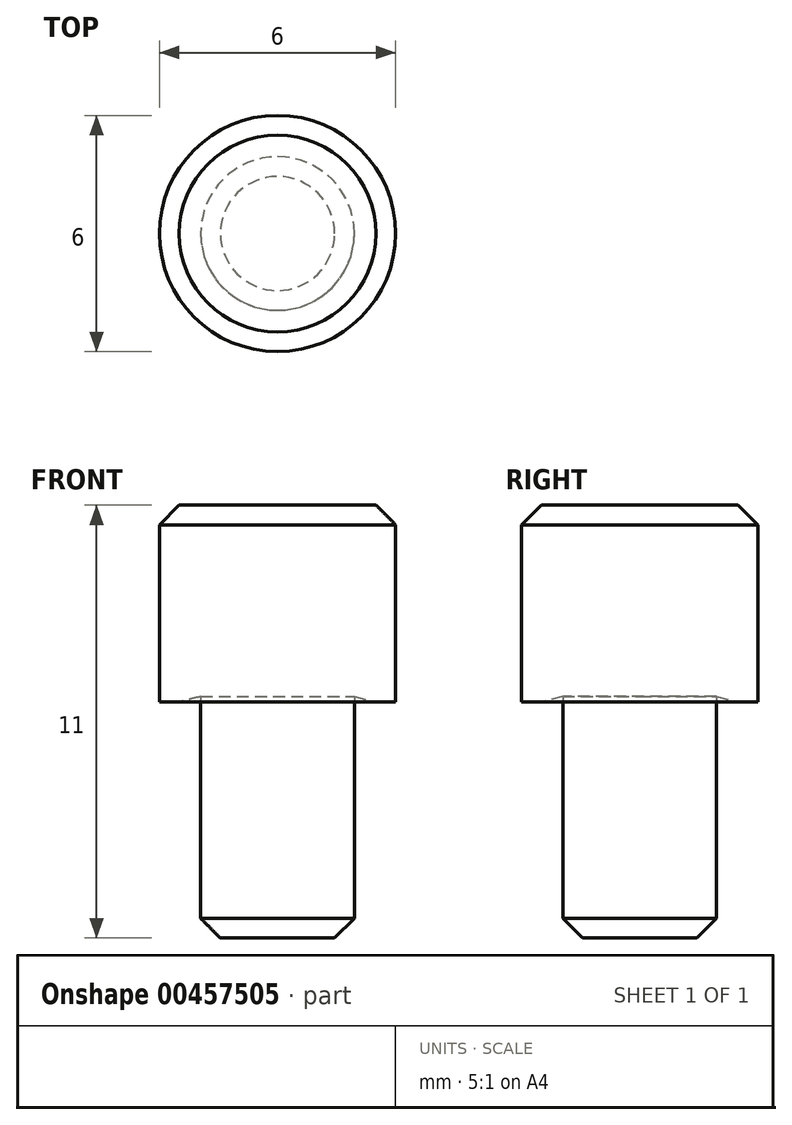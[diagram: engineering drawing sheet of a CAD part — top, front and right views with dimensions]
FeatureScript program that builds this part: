
annotation { "Feature Type Name" : "Feature", "Feature Type Description" : "" }
export const myFeature = defineFeature(function(context is Context, id is Id, definition is map)
    precondition{}
    {
        {
            var Q0;
            Q0=qCreatedBy(makeId("Front.planeOp"),FACE);
            var sketch = newSketch(context, id + "F0", { "sketchPlane" : qUnion([Q0])});
            skLineSegment(sketch, "E0.bottom", {"start": v(1.95, 0) * mm, "end": v(0, 0) * mm});
            skLineSegment(sketch, "E0.left", {"start": v(1.95, 0) * mm, "end": v(1.95, 6) * mm});
            skLineSegment(sketch, "E1.bottom", {"start": v(0, 11) * mm, "end": v(3, 11) * mm});
            skLineSegment(sketch, "E1.right", {"start": v(3, 11) * mm, "end": v(3, 6) * mm});
            skPoint(sketch, "E2", {"position": v(0, 11) * mm});
            skPoint(sketch, "E3", {"position": v(0, 0) * mm});
            skLineSegment(sketch, "E4.trimOffspring", {"start": v(1.95, 6) * mm, "end": v(3, 6) * mm});
            skLineSegment(sketch, "E5", {"start": v(0, 18.37) * mm, "end": v(0, -7.66) * mm});
            skSolve(sketch);
        }
        {
            var Q0;
            {var subQ1=sQuery(id+"F0.wireOp",EDGE,"E0.bottom");Q0=makeQuery(id+"F0.imprint","IMPRINT",FACE,{"disambiguationData":[TD([[makeQuery(id+"F0.imprint","IMPRINT",EDGE,{"derivedFrom":subQ1}),-1.0]])]});}
            var Q1;
            Q1=sQuery(id+"F0.wireOp",EDGE,"E5");
            revolve(context, id + "F1", {"entities" : qUnion([Q0]), "axis" : qUnion([Q1]), "revolveType" : RevolveType.FULL});
        }
        {
            var Q0;
            Q0=makeQuery(id+"F1.opRevolve","SWEPT_EDGE",EDGE,{"disambiguationData":[OSD([sQuery(id+"F0.wireOp",EDGE,"E1.bottom"),sQuery(id+"F0.wireOp",EDGE,"E1.right")])]});
            var Q1;
            Q1=makeQuery(id+"F1.opRevolve","SWEPT_FACE",FACE,{"disambiguationData":[OSD([sQuery(id+"F0.wireOp",EDGE,"E0.bottom")])]});
            chamfer(context, id + "F2", {"entities" : qUnion([Q0, Q1]), "width" : 0.5 * mm, "tangentPropagation" : true});
        }
        {
            var Q0;
            Q0=qCreatedBy(makeId("Front.planeOp"),FACE);
            var sketch = newSketch(context, id + "F3", { "sketchPlane" : qUnion([Q0])});
            skPoint(sketch, "E6", {"position": v(1.95, 6) * mm});
            skLineSegment(sketch, "E7", {"start": v(2.5, 6) * mm, "end": v(1.95, 6) * mm});
            skLineSegment(sketch, "E8", {"start": v(2.5, 6) * mm, "end": v(1.95, 6.14) * mm});
            skLineSegment(sketch, "E9", {"start": v(1.95, 6) * mm, "end": v(1.95, 6.14) * mm});
            skLineSegment(sketch, "E10", {"start": v(0, 12.66) * mm, "end": v(0, -1.84) * mm});
            skSolve(sketch);
        }
        {
            var Q0;
            Q0=qSketchRegion(id+"F3",true);
            var Q1;
            Q1=sQuery(id+"F3.wireOp",EDGE,"E10");
            revolve(context, id + "F4", {"operationType" : NewBodyOperationType.REMOVE, "entities" : qUnion([Q0]), "axis" : qUnion([Q1]), "revolveType" : RevolveType.FULL, "oppositeDirection" : true});
        }
    });
